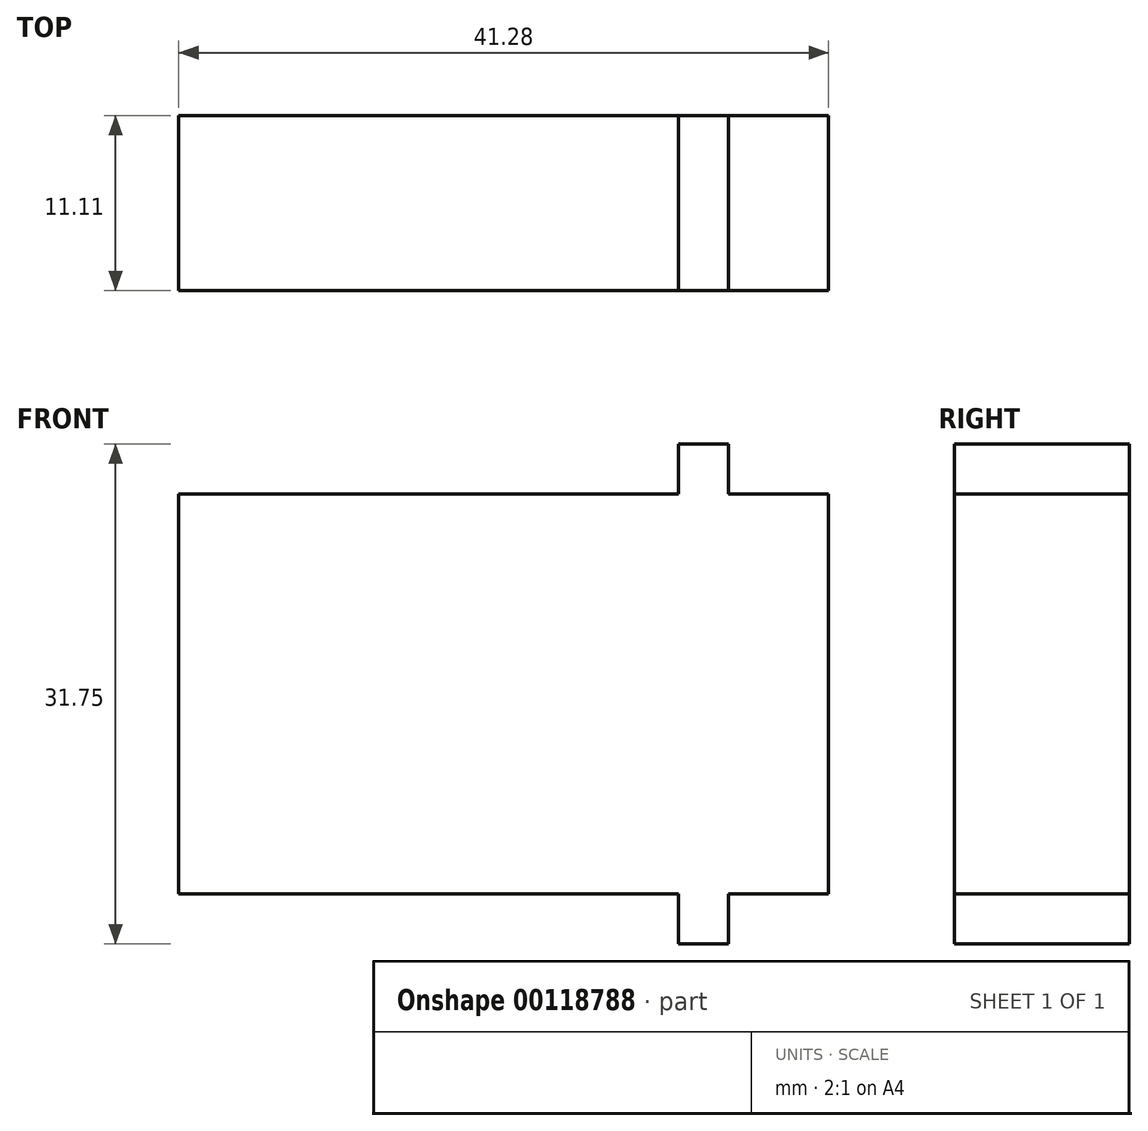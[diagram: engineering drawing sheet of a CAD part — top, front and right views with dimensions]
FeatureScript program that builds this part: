
annotation { "Feature Type Name" : "Feature", "Feature Type Description" : "" }
export const myFeature = defineFeature(function(context is Context, id is Id, definition is map)
    precondition{}
    {
        {
            var Q0;
            Q0=qCreatedBy(makeId("Front.planeOp"),FACE);
            var sketch = newSketch(context, id + "F0", { "sketchPlane" : qUnion([Q0])});
            skLineSegment(sketch, "E0.bottom", {"start": v(-29.48, -17.4) * mm, "end": v(2.27, -17.4) * mm});
            skLineSegment(sketch, "E0.top", {"start": v(-29.48, -42.8) * mm, "end": v(2.27, -42.8) * mm});
            skLineSegment(sketch, "E0.left", {"start": v(-29.48, -17.4) * mm, "end": v(-29.48, -42.8) * mm});
            skLineSegment(sketch, "E0.right", {"start": v(2.27, -17.4) * mm, "end": v(2.27, -42.8) * mm});
            skSolve(sketch);
        }
        {
            var Q0;
            Q0=makeQuery(id+"F0.imprint","IMPRINT",FACE,{"disambiguationData":[TD([[makeQuery(id+"F0.imprint","IMPRINT",EDGE,{"derivedFrom":sQuery(id+"F0.wireOp",EDGE,"E0.bottom")}),-1.0]])]});
            extrude(context, id + "F1", {"entities" : qUnion([Q0]), "depth" : 11.1 * mm});
        }
        {
            var Q0;
            Q0=makeQuery(id+"F1.opExtrude","SWEPT_FACE",FACE,{"disambiguationData":[OSD([sQuery(id+"F0.wireOp",EDGE,"E0.right")])]});
            var sketch = newSketch(context, id + "F2", { "sketchPlane" : qUnion([Q0])});
            skLineSegment(sketch, "E1.bottom", {"start": v(-11.11, -14.23) * mm, "end": v(0, -14.23) * mm});
            skLineSegment(sketch, "E1.top", {"start": v(-11.11, -45.98) * mm, "end": v(0, -45.98) * mm});
            skLineSegment(sketch, "E1.left", {"start": v(-11.11, -14.23) * mm, "end": v(-11.11, -45.98) * mm});
            skLineSegment(sketch, "E1.right", {"start": v(0, -14.23) * mm, "end": v(0, -45.98) * mm});
            skSolve(sketch);
        }
        {
            var Q0;
            Q0 = qSketchRegion(id + "F2", true);
            extrude(context, id + "F3", {"entities" : qUnion([Q0]), "operationType" : NewBodyOperationType.ADD, "depth" : 3.17 * mm});
        }
        {
            var Q0;
            Q0=makeQuery(id+"F3.opExtrude","CAP_FACE",FACE,{"disambiguationData":[OSD([sQuery(id+"F2.wireOp",EDGE,"E1.bottom"),sQuery(id+"F2.wireOp",EDGE,"E1.top"),sQuery(id+"F2.wireOp",EDGE,"E1.left"),sQuery(id+"F2.wireOp",EDGE,"E1.right")])],"isStart":false});
            var sketch = newSketch(context, id + "F4", { "sketchPlane" : qUnion([Q0])});
            skLineSegment(sketch, "E2.bottom", {"start": v(-11.11, -17.4) * mm, "end": v(0, -17.4) * mm});
            skLineSegment(sketch, "E2.top", {"start": v(-11.11, -42.8) * mm, "end": v(0, -42.8) * mm});
            skLineSegment(sketch, "E2.left", {"start": v(-11.11, -17.4) * mm, "end": v(-11.11, -42.8) * mm});
            skLineSegment(sketch, "E2.right", {"start": v(0, -17.4) * mm, "end": v(0, -42.8) * mm});
            skSolve(sketch);
        }
        {
            var Q0;
            Q0=makeQuery(id+"F4.imprint","IMPRINT",FACE,{"disambiguationData":[TD([[makeQuery(id+"F4.imprint","IMPRINT",EDGE,{"derivedFrom":sQuery(id+"F4.wireOp",EDGE,"E2.bottom")}),-1.0]])]});
            extrude(context, id + "F5", {"entities" : qUnion([Q0]), "operationType" : NewBodyOperationType.ADD, "depth" : 6.35 * mm});
        }
    });
